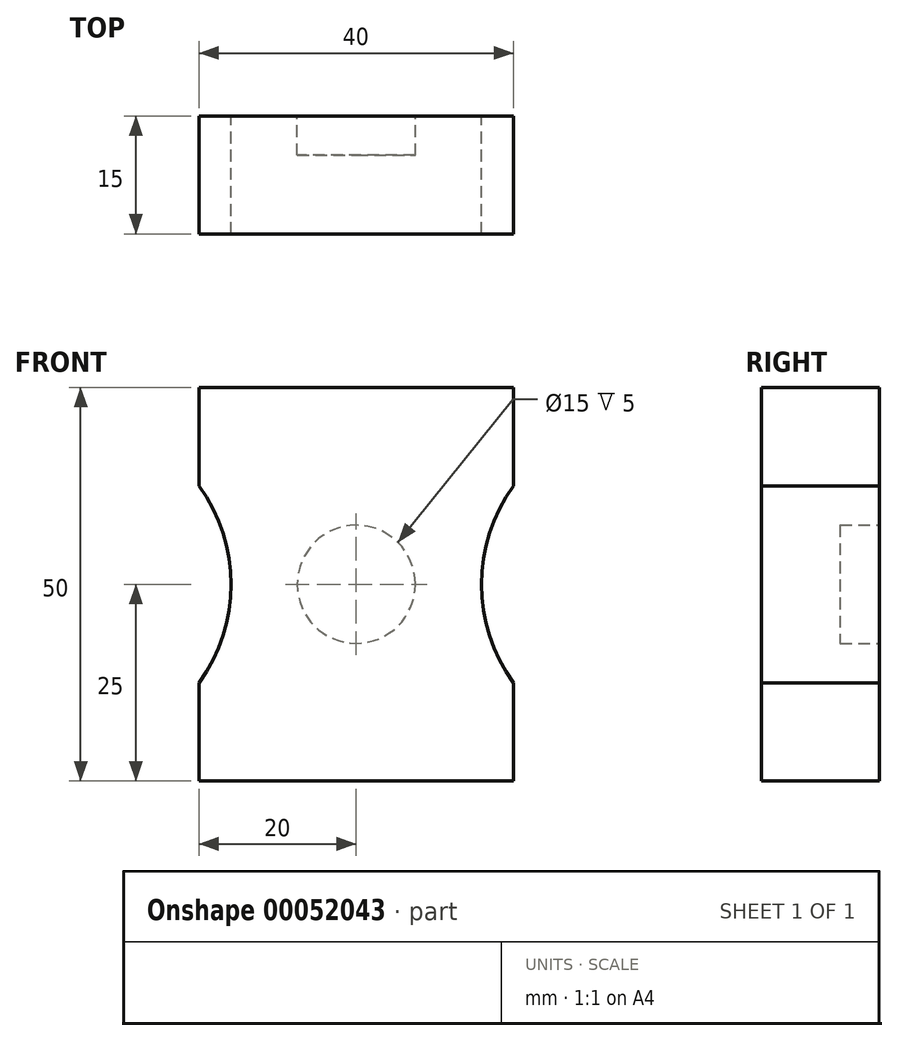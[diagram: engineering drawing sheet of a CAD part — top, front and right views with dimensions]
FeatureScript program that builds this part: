
annotation { "Feature Type Name" : "Feature", "Feature Type Description" : "" }
export const myFeature = defineFeature(function(context is Context, id is Id, definition is map)
    precondition{}
    {
        {
            var Q0;
            Q0=qCreatedBy(makeId("Front.planeOp"),FACE);
            var sketch = newSketch(context, id + "F0", { "sketchPlane" : qUnion([Q0])});
            skLineSegment(sketch, "E0.rect.bottom", {"start": v(20, -25) * mm, "end": v(-20, -25) * mm});
            skLineSegment(sketch, "E0.rect.top", {"start": v(20, 25) * mm, "end": v(-20, 25) * mm});
            skLineSegment(sketch, "E0.rect.left", {"start": v(20, -25) * mm, "end": v(20, -12.54) * mm});
            skLineSegment(sketch, "E0.rect.right", {"start": v(-20, -25) * mm, "end": v(-20, -12.54) * mm});
            skPoint(sketch, "E0.rect.middle", {"position": v(0, 0) * mm});
            skLineSegment(sketch, "E1", {"start": v(-20, 0) * mm, "end": v(20, 0) * mm, "construction": true});
            skLineSegment(sketch, "E2", {"start": v(-20, 12.5) * mm, "end": v(20, 12.5) * mm, "construction": true});
            skArc(sketch, "E3", {"start": v(-20, -12.54) * mm, "mid": v(-15.92, -0.02) * mm, "end": v(-20, 12.5) * mm});
            skArc(sketch, "E4.MirrorCS", {"start": v(20, -12.54) * mm, "mid": v(15.92, -0.02) * mm, "end": v(20, 12.5) * mm});
            skLineSegment(sketch, "E5.trimOffspring", {"start": v(-20, 12.5) * mm, "end": v(-20, 25) * mm});
            skLineSegment(sketch, "E6.trimOffspring", {"start": v(20, 12.5) * mm, "end": v(20, 25) * mm});
            skSolve(sketch);
        }
        {
            var Q0;
            Q0 = qSketchRegion(id + "F0", true);
            extrude(context, id + "F1", {"entities" : qUnion([Q0]), "depth" : 15 * mm});
        }
        {
            var Q0;
            Q0=makeQuery(id+"F1.opExtrude","CAP_FACE",FACE,{"disambiguationData":[OSD([sQuery(id+"F0.wireOp",EDGE,"E0.rect.bottom"),sQuery(id+"F0.wireOp",EDGE,"E0.rect.top"),sQuery(id+"F0.wireOp",EDGE,"E0.rect.left"),sQuery(id+"F0.wireOp",EDGE,"E0.rect.right"),sQuery(id+"F0.wireOp",EDGE,"E3"),sQuery(id+"F0.wireOp",EDGE,"E4.MirrorCS"),sQuery(id+"F0.wireOp",EDGE,"E5.trimOffspring"),sQuery(id+"F0.wireOp",EDGE,"E6.trimOffspring")])],"isStart":true});
            var sketch = newSketch(context, id + "F2", { "sketchPlane" : qUnion([Q0])});
            skCircle(sketch, "E7", {"center": v(0, 0) * mm, "radius": 7.5 * mm});
            skSolve(sketch);
        }
        {
            var Q0;
            Q0 = qSketchRegion(id + "F2", true);
            extrude(context, id + "F3", {"entities" : qUnion([Q0]), "operationType" : NewBodyOperationType.REMOVE, "oppositeDirection" : true, "depth" : 5 * mm});
        }
    });
